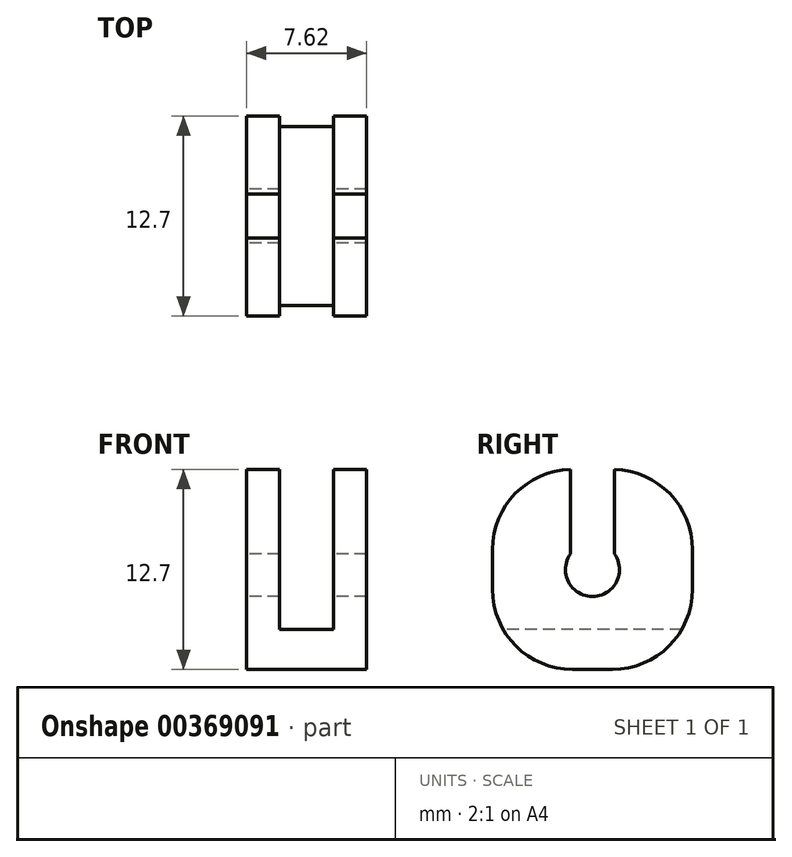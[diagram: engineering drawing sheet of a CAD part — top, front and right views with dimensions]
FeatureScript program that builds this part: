
annotation { "Feature Type Name" : "Feature", "Feature Type Description" : "" }
export const myFeature = defineFeature(function(context is Context, id is Id, definition is map)
    precondition{}
    {
        {
            var Q0;
            Q0=qCreatedBy(makeId("Top.planeOp"),FACE);
            var sketch = newSketch(context, id + "F0", { "sketchPlane" : qUnion([Q0])});
            skLineSegment(sketch, "E0.bottom", {"start": v(-66.06, 27.1) * mm, "end": v(-58.44, 27.1) * mm});
            skLineSegment(sketch, "E0.top", {"start": v(-66.06, 14.4) * mm, "end": v(-58.44, 14.4) * mm});
            skLineSegment(sketch, "E0.left", {"start": v(-66.06, 27.1) * mm, "end": v(-66.06, 14.4) * mm});
            skLineSegment(sketch, "E0.right", {"start": v(-58.44, 27.1) * mm, "end": v(-58.44, 14.4) * mm});
            skSolve(sketch);
        }
        {
            var Q0;
            Q0 = qSketchRegion(id + "F0", true);
            extrude(context, id + "F1", {"entities" : qUnion([Q0]), "depth" : 12.7 * mm});
        }
        {
            var Q0;
            Q0=makeQuery(id+"F1.opExtrude","SWEPT_FACE",FACE,{"disambiguationData":[OSD([sQuery(id+"F0.wireOp",EDGE,"E0.left")])]});
            var sketch = newSketch(context, id + "F2", { "sketchPlane" : qUnion([Q0])});
            skCircle(sketch, "E1", {"center": v(-20.74, 6.35) * mm, "radius": 1.71 * mm});
            skPoint(sketch, "E1.centerSnap0", {"position": v(-20.74, 12.7) * mm});
            skPoint(sketch, "E1.centerSnap1", {"position": v(-27.1, 6.35) * mm});
            skSolve(sketch);
        }
        {
            var Q0;
            Q0 = qSketchRegion(id + "F2", true);
            extrude(context, id + "F3", {"entities" : qUnion([Q0]), "operationType" : NewBodyOperationType.REMOVE, "oppositeDirection" : true, "depth" : 25.4 * mm});
        }
        {
            var Q0;
            Q0=makeQuery(id+"F1.opExtrude","SWEPT_FACE",FACE,{"disambiguationData":[OSD([sQuery(id+"F0.wireOp",EDGE,"E0.left")])]});
            var sketch = newSketch(context, id + "F4", { "sketchPlane" : qUnion([Q0])});
            skLineSegment(sketch, "E2.bottom", {"start": v(-22.14, 9.93) * mm, "end": v(-19.34, 9.93) * mm});
            skLineSegment(sketch, "E2.top", {"start": v(-22.14, 15.47) * mm, "end": v(-19.34, 15.47) * mm});
            skLineSegment(sketch, "E2.right", {"start": v(-19.34, 9.93) * mm, "end": v(-19.34, 15.47) * mm});
            skPoint(sketch, "E2.middle", {"position": v(-20.74, 12.7) * mm});
            skLineSegment(sketch, "E3", {"start": v(-22.14, 15.47) * mm, "end": v(-22.14, 7.34) * mm});
            skLineSegment(sketch, "E4", {"start": v(-22.14, 7.34) * mm, "end": v(-19.34, 7.34) * mm});
            skLineSegment(sketch, "E5", {"start": v(-19.34, 7.34) * mm, "end": v(-19.34, 9.93) * mm});
            skSolve(sketch);
        }
        {
            var Q0;
            Q0 = qSketchRegion(id + "F4", true);
            extrude(context, id + "F5", {"entities" : qUnion([Q0]), "operationType" : NewBodyOperationType.REMOVE, "oppositeDirection" : true, "depth" : 25.4 * mm});
        }
        {
            var Q0;
            {var subQ0=sQuery(id+"F0.wireOp",EDGE,"E0.bottom");var subQ1=sQuery(id+"F0.wireOp",EDGE,"E0.right");var subQ2=sQuery(id+"F0.wireOp",EDGE,"E0.left");Q0=makeQuery(id+"F5.boolean.opBoolean","SPLIT",FACE,{"disambiguationData":[TD([makeQuery(id+"F1.opExtrude","SWEPT_FACE",FACE,{"disambiguationData":[OSD([subQ0])]})])],"derivedFrom":makeQuery(id+"F1.opExtrude","CAP_FACE",FACE,{"disambiguationData":[OSD([subQ0,sQuery(id+"F0.wireOp",EDGE,"E0.top"),subQ2,subQ1])],"isStart":false})});}
            var sketch = newSketch(context, id + "F6", { "sketchPlane" : qUnion([Q0])});
            skLineSegment(sketch, "E6.0.0", {"start": v(-58.44, 19.34) * mm, "end": v(-66.06, 19.34) * mm});
            skLineSegment(sketch, "E6.0.1", {"start": v(-66.06, 19.34) * mm, "end": v(-66.06, 14.4) * mm});
            skLineSegment(sketch, "E6.0.2", {"start": v(-66.06, 14.4) * mm, "end": v(-58.44, 14.4) * mm});
            skLineSegment(sketch, "E6.0.3", {"start": v(-58.44, 14.4) * mm, "end": v(-58.44, 19.34) * mm});
            skLineSegment(sketch, "E7.bottom", {"start": v(-60.54, 27.1) * mm, "end": v(-63.97, 27.1) * mm});
            skLineSegment(sketch, "E7.top", {"start": v(-60.54, 11.6) * mm, "end": v(-63.97, 11.6) * mm});
            skLineSegment(sketch, "E7.left", {"start": v(-60.54, 27.1) * mm, "end": v(-60.54, 11.6) * mm});
            skLineSegment(sketch, "E7.right", {"start": v(-63.97, 27.1) * mm, "end": v(-63.97, 11.6) * mm});
            skPoint(sketch, "E7.middle", {"position": v(-62.25, 19.34) * mm});
            skSolve(sketch);
        }
        {
            var Q0;
            {var subQ5=sQuery(id+"F6.wireOp",EDGE,"E7.top");Q0=makeQuery(id+"F6.imprint","IMPRINT",FACE,{"disambiguationData":[TD([[makeQuery(id+"F6.imprint","IMPRINT",EDGE,{"derivedFrom":subQ5}),-1.0]])]});}
            var Q1;
            {var subQ0=sQuery(id+"F6.wireOp",EDGE,"E7.left");var subQ1=sQuery(id+"F6.wireOp",EDGE,"E6.0.0");var subQ2=makeQuery(id+"F6.imprint","INTERSECT",VERTEX,{"derivedFrom":[subQ1,subQ0]});Q1=makeQuery(id+"F6.imprint","IMPRINT",FACE,{"disambiguationData":[TD([[makeQuery(id+"F6.imprint","IMPRINT",EDGE,{"disambiguationData":[TD([[subQ2,-1.0]])],"derivedFrom":subQ1}),1.0]])]});}
            var Q2;
            {var subQ0=sQuery(id+"F6.wireOp",EDGE,"E7.left");var subQ1=sQuery(id+"F6.wireOp",EDGE,"E6.0.0");var subQ2=makeQuery(id+"F6.imprint","INTERSECT",VERTEX,{"derivedFrom":[subQ1,subQ0]});Q2=makeQuery(id+"F6.imprint","IMPRINT",FACE,{"disambiguationData":[TD([[makeQuery(id+"F6.imprint","IMPRINT",EDGE,{"disambiguationData":[TD([[subQ2,-1.0]])],"derivedFrom":subQ1}),-1.0]])]});}
            var Q3;
            {var subQ0=sQuery(id+"F6.wireOp",EDGE,"E7.bottom");Q3=makeQuery(id+"F6.imprint","IMPRINT",FACE,{"disambiguationData":[TD([[makeQuery(id+"F6.imprint","IMPRINT",EDGE,{"derivedFrom":subQ0}),-1.0]])]});}
            extrude(context, id + "F7", {"entities" : qUnion([Q0, Q1, Q2, Q3]), "operationType" : NewBodyOperationType.REMOVE, "oppositeDirection" : true, "depth" : 10.16 * mm});
        }
        {
            var Q0;
            Q0=makeQuery(id+"F1.opExtrude","CAP_EDGE",EDGE,{"disambiguationData":[OSD([sQuery(id+"F0.wireOp",EDGE,"E0.top")])],"isStart":true});
            var Q1;
            Q1=makeQuery(id+"F1.opExtrude","CAP_EDGE",EDGE,{"disambiguationData":[OSD([sQuery(id+"F0.wireOp",EDGE,"E0.bottom")])],"isStart":true});
            var Q2;
            {var subQ0=sQuery(id+"F0.wireOp",EDGE,"E0.bottom");var subQ1=sQuery(id+"F0.wireOp",EDGE,"E0.left");Q2=makeQuery(id+"F7.boolean.opBoolean","SPLIT",EDGE,{"disambiguationData":[TD([makeQuery(id+"F1.opExtrude","SWEPT_FACE",FACE,{"disambiguationData":[OSD([subQ1])]})])],"derivedFrom":makeQuery(id+"F1.opExtrude","CAP_EDGE",EDGE,{"disambiguationData":[OSD([subQ0])],"isStart":false})});}
            var Q3;
            {var subQ0=sQuery(id+"F0.wireOp",EDGE,"E0.left");var subQ1=sQuery(id+"F0.wireOp",EDGE,"E0.top");Q3=makeQuery(id+"F7.boolean.opBoolean","SPLIT",EDGE,{"disambiguationData":[TD([makeQuery(id+"F1.opExtrude","SWEPT_FACE",FACE,{"disambiguationData":[OSD([subQ0])]})])],"derivedFrom":makeQuery(id+"F1.opExtrude","CAP_EDGE",EDGE,{"disambiguationData":[OSD([subQ1])],"isStart":false})});}
            var Q4;
            {var subQ0=sQuery(id+"F0.wireOp",EDGE,"E0.bottom");var subQ1=sQuery(id+"F0.wireOp",EDGE,"E0.right");Q4=makeQuery(id+"F7.boolean.opBoolean","SPLIT",EDGE,{"disambiguationData":[TD([makeQuery(id+"F1.opExtrude","SWEPT_FACE",FACE,{"disambiguationData":[OSD([subQ1])]})])],"derivedFrom":makeQuery(id+"F1.opExtrude","CAP_EDGE",EDGE,{"disambiguationData":[OSD([subQ0])],"isStart":false})});}
            var Q5;
            {var subQ0=sQuery(id+"F0.wireOp",EDGE,"E0.right");var subQ1=sQuery(id+"F0.wireOp",EDGE,"E0.top");Q5=makeQuery(id+"F7.boolean.opBoolean","SPLIT",EDGE,{"disambiguationData":[TD([makeQuery(id+"F1.opExtrude","SWEPT_FACE",FACE,{"disambiguationData":[OSD([subQ0])]})])],"derivedFrom":makeQuery(id+"F1.opExtrude","CAP_EDGE",EDGE,{"disambiguationData":[OSD([subQ1])],"isStart":false})});}
            fillet(context, id + "F8", {"entities" : qUnion([Q0, Q1, Q2, Q3, Q4, Q5]), "radius" : 5.08 * mm, "tangentPropagation" : true, "allowEdgeOverflow" : false});
        }
    });
